# Revit family: Tub_Spout-Wall_Mounted-Waterworks-Flyte
name_source: partatom
category: Plumbing Fixtures
revit_build: Autodesk Revit MEP 2014 (Build: 20140709_2115(x64)
units: mm (PartAtom-declared; Revit-internal decimal feet)

## types (4) — shared parameters
ADA Compliant = Yes
Anti-scald Protection = No
Assembly Code = D2010
CW Connection = Yes
Certification IAPMO = Yes
Certification State of MA = Yes
Certification cUPC = Yes
Code Compliance = Code # FLTU80:
Default Elevation = 2' - 10"
Depth = 0' - 7 15/16"
Fittings Hole Diameter = 0' - 1 1/4"
HW Connection = Yes
Height = 0' - 2 3/4"
Hot Limit Safety Stop = No
Inlet Connection Diameter = 0' - 0 1/2"
Keynote = 22 40 00
Length = 0' - 2 3/8"
Manufacturer = Waterworks
Model = FLTS80
Pressure = 45.00 psi
Product Documentation Link = http://assets.waterworks.com
Product Page URL = http://www.waterworks.com
Spout Reach = 0' - 7 5/16"
URL = http://www.waterworks.com
Vent Connection = No
Version = 2014 - v1.0a
Warranty = http://www.waterworks.com
Waste Connection = No
Water Connector = Inlet - Female NPT
‌Installation Requirements or Notes = Unrestricted flow of approximately 12 gallons per minute (gpm)
zero-valued in all types: CWFU, HWFU, WFU

## per-type parameters (varying)
| type | Constraint | Description | Finish | Model SKU | Product Name |
| Chrome | 1 | Wall Mounted Tub Spout in Chrome, Fixed Spray | Metal - Waterworks - Chrome | 09-48141-36049 | Flyte Wall Mounted Tub Spout in Chrome |
| Graphite | 2 | Wall Mounted Tub Spout in Graphite, Fixed Spray | Metal - Waterworks - Graphite | 09-57398-71693 | Flyte Wall Mounted Tub Spout in Graphite |
| Nickel | 3 | Wall Mounted Tub Spout in Nickel, Fixed Spray | Metal - Waterworks - Nickel | 09-67403-14558 | Flyte Wall Mounted Tub Spout in Nickel |
| Unlacquered Brass | 4 | Wall Mounted Tub Spout in Unlacquered Brass, Fixed Spray | Metal - Waterworks - Unlacquered Brass | 09-03793-57470 | Flyte Wall Mounted Tub Spout in Unlacquered Brass |

## geometry (parser evidence)
native form markers: Sweep x6
no freeform markers — native parametric forms only
